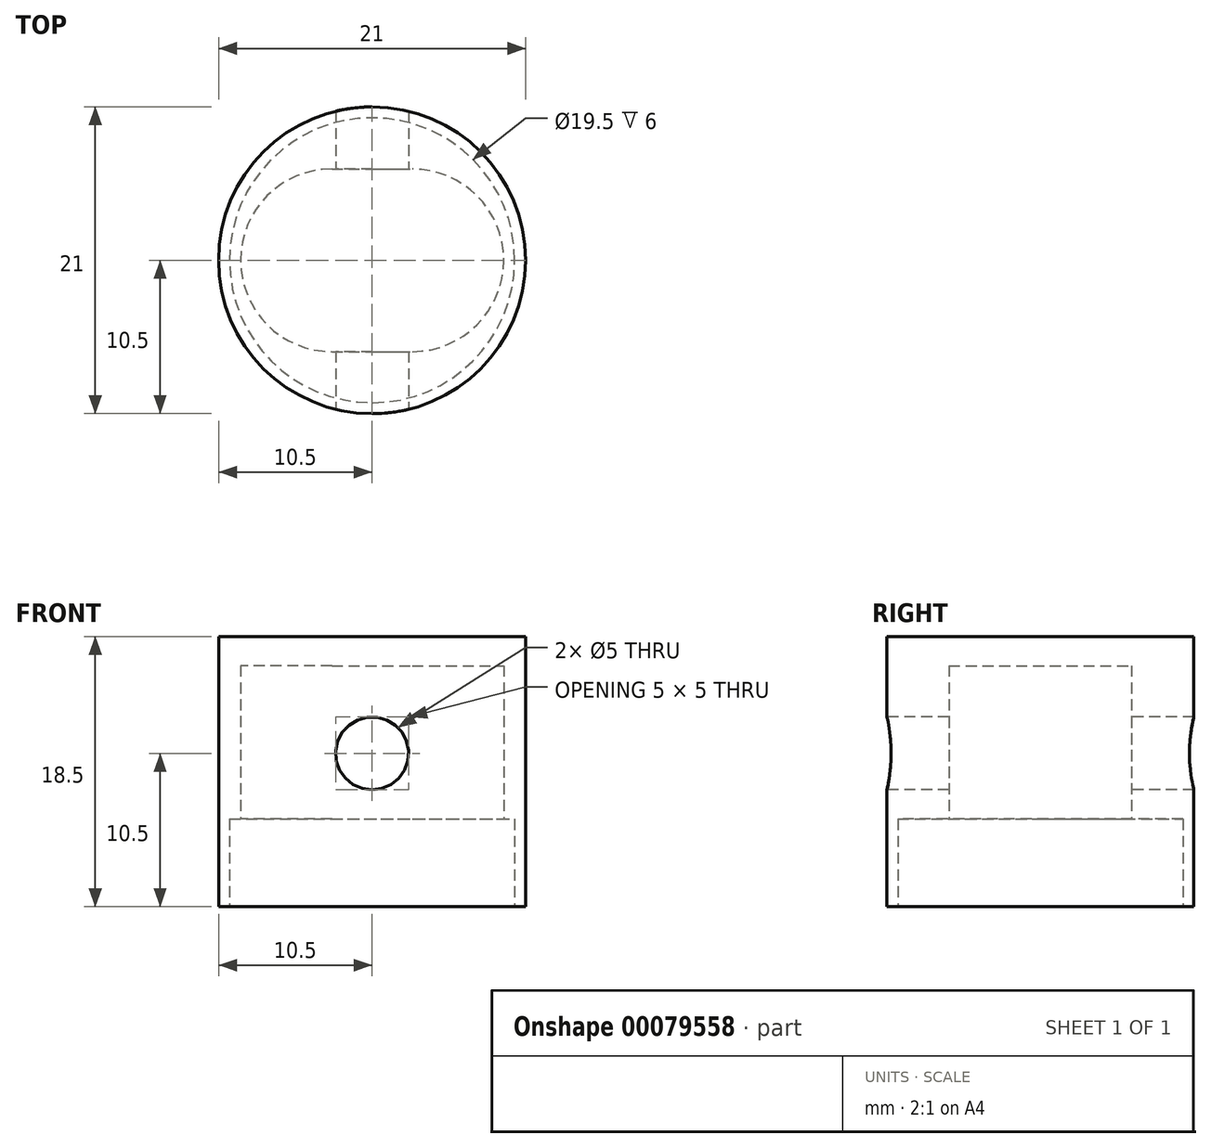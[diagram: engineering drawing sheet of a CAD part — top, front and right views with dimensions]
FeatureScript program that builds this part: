
annotation { "Feature Type Name" : "Feature", "Feature Type Description" : "" }
export const myFeature = defineFeature(function(context is Context, id is Id, definition is map)
    precondition{}
    {
        {
            var Q0;
            Q0=qCreatedBy(makeId("Top.planeOp"),FACE);
            var sketch = newSketch(context, id + "F0", { "sketchPlane" : qUnion([Q0])});
            skCircle(sketch, "E0", {"center": v(0, 0) * mm, "radius": 10.5 * mm});
            skSolve(sketch);
        }
        {
            var Q0;
            Q0=makeQuery(id+"F0.imprint","IMPRINT",FACE,{"disambiguationData":[TD([[makeQuery(id+"F0.imprint","IMPRINT",EDGE,{"derivedFrom":sQuery(id+"F0.wireOp",EDGE,"E0")}),1.0]])]});
            extrude(context, id + "F1", {"entities" : qUnion([Q0]), "depth" : 18.5 * mm});
        }
        {
            var Q0;
            Q0=makeQuery(id+"F1.opExtrude","CAP_FACE",FACE,{"disambiguationData":[OSD([sQuery(id+"F0.wireOp",EDGE,"E0")])],"isStart":true});
            var sketch = newSketch(context, id + "F2", { "sketchPlane" : qUnion([Q0])});
            skArc(sketch, "E1", {"start": v(-2.75, 6.25) * mm, "mid": v(-9, 0) * mm, "end": v(-2.75, -6.25) * mm});
            skArc(sketch, "E2", {"start": v(2.75, -6.25) * mm, "mid": v(9, 0) * mm, "end": v(2.75, 6.25) * mm});
            skLineSegment(sketch, "E3", {"start": v(-2.75, 6.25) * mm, "end": v(2.75, 6.25) * mm});
            skLineSegment(sketch, "E4", {"start": v(-2.75, -6.25) * mm, "end": v(2.75, -6.25) * mm});
            skSolve(sketch);
        }
        {
            var Q0;
            Q0=makeQuery(id+"F2.imprint","IMPRINT",FACE,{"disambiguationData":[TD([[makeQuery(id+"F2.imprint","IMPRINT",EDGE,{"derivedFrom":sQuery(id+"F2.wireOp",EDGE,"E1")}),1.0]])]});
            extrude(context, id + "F3", {"entities" : qUnion([Q0]), "operationType" : NewBodyOperationType.REMOVE, "oppositeDirection" : true, "depth" : 16.5 * mm});
        }
        {
            var Q0;
            Q0=makeQuery(id+"F1.opExtrude","CAP_FACE",FACE,{"disambiguationData":[OSD([sQuery(id+"F0.wireOp",EDGE,"E0")])],"isStart":true});
            var sketch = newSketch(context, id + "F4", { "sketchPlane" : qUnion([Q0])});
            skCircle(sketch, "E5", {"center": v(0, 0) * mm, "radius": 9.75 * mm});
            skSolve(sketch);
        }
        {
            var Q0;
            Q0=makeQuery(id+"F4.imprint","IMPRINT",FACE,{"disambiguationData":[TD([[makeQuery(id+"F4.imprint","IMPRINT",EDGE,{"derivedFrom":sQuery(id+"F4.wireOp",EDGE,"E5")}),1.0]])]});
            extrude(context, id + "F5", {"entities" : qUnion([Q0]), "operationType" : NewBodyOperationType.REMOVE, "oppositeDirection" : true, "depth" : 6 * mm});
        }
        {
            var Q0;
            Q0=qCreatedBy(makeId("Front.planeOp"),FACE);
            var sketch = newSketch(context, id + "F6", { "sketchPlane" : qUnion([Q0])});
            skCircle(sketch, "E6", {"center": v(0, 10.5) * mm, "radius": 2.5 * mm});
            skSolve(sketch);
        }
        {
            var Q0;
            Q0 = qSketchRegion(id + "F6", true);
            extrude(context, id + "F7", {"entities" : qUnion([Q0]), "operationType" : NewBodyOperationType.REMOVE, "endBound" : BoundingType.THROUGH_ALL, "oppositeDirection" : true, "depth" : 25 * mm, "hasSecondDirection" : true, "secondDirectionBound" : SecondDirectionBoundingType.THROUGH_ALL, "secondDirectionOppositeDirection" : false, "secondDirectionDepth" : 25 * mm});
        }
    });
